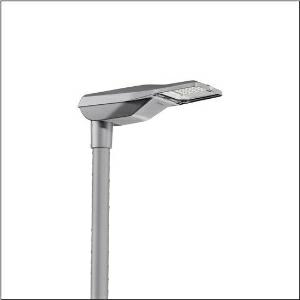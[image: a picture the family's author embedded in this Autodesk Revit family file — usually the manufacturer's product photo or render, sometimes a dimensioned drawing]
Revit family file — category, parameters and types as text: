
# Revit family: streetlight_sl_21_iq_micro___st0_8a_5xe1c31d08db_b6ee
name_source: partatom
category: Lighting Fixtures
units: mm (PartAtom-declared; Revit-internal decimal feet)

## family parameters
Cut with Voids When Loaded = No
Host = Face
Light Source = No
Part Type = Normal
Room Calculation Point = No
Round Connector Dimension = Use Diameter
Shared = No

## types (1)
- --- (1 x LED, 4810 lm, 36.4 W, 3000K)
    Apparent Load = 36 VA
    CIE Flux Codes = 38 75 97 100 100
    Color Rendering = 70
    Color Temperature = 3000K
    Default Elevation = 1800 mm
    Description = Streetlight SL 21 iQ micro, mast luminaire, primary light control with lens, of PMMA, primary optical cover: cover, of toughened safety glass, transparent, light distribution: ST0.8a, light emission: direct distribution, primary light characteristic: asymmetric, installation type: post-top, side-entry, LED, High Power LED, rated luminous flux: 4.810lm, luminous efficacy: 132lm/W, light colour: 730, colour temperature: 3000K, control gear: iQ-Comfort, control: Auto-Match, Temp-Guard, Lumen-Switch, Night-Set, Smart-Wire, Light-Fading, Desk-Remote (wireless, voltage-free reading and setting of iQ features in the workshop via application-optimized NFC function/RFID function), optimised constant luminous flux control (CLO 2.0), pre-setting: linear dimming characteristic, mains connection: 220..240V, AC, 50/60Hz, start of lifetime: 36W, end of service life: 38W, reduction: 16W, luminaire housing, of diecast aluminium, powder-coated, Siteco® metallic grey (DB 702S), corrosivity category C5 mid according to DIN EN ISO 12944, please order mast flange separately, inclination adjustable: 0°, 5°, 10°, 15°, sealing non-destructively replaceable, multi-level sealing system, length: 528mm, width: 235mm, height: 110mm, mast flange for spigot size: 42mm (side-entry): 5XC10008XM4, 60/48mm (side-entry/post-top): 5XC10108XM2, 76/60mm (side-entry/post-top): 5XC10108XM1, protection rating (complete): IP66, insulation class (complete): insulation class II (safety insulation), certification: CE, ENEC, ENEC+, VDE, impact resistance: IK10, permissible operating ambient temperature for outdoor applications: -40..+50°C, standard-compliant lighting for roads and squares, packaging unit: 1 piece

Light Distribution: ST0.8a
    Height = 110 mm
    Lamp = 1 x LED
    Lamp Light Flux = 4810 lm
    Lamp Power = 36.4 W
    Lamp count = 1
    Length = 528 mm
    Luminous efficacy = 132 lm/W
    Manufacturer = Siteco
    ModVariant = No
    Model = 5XE1C31D08DB
    Number of Poles = 1
    OnlyDefault = Yes
    Power Factor = 1
    Product Name = Streetlight SL 21 iQ micro | ST0.8a
    Product group = mast luminaire | pylon top
    ProductGroupID = 6100
    Protection Class = Protection class II
    Protection Degree = IP 66
    RLX_Detail_Level = 1
    RLX_Emergency_Light_Flux = 0 lm
    RLX_Emergency_Type = 0
    RLX_Emergency_Type_DB = No
    RlxData = <blob elided: 98957 chars, md5=221f48d3>
    Socket = socket
    Standby Power = 0 W
    System Light Flux = 4810 lm
    System Power = 36 W
    Type Comments = factory setting: luminous flux: 100 % | dim-lin: 254 | 715 mA
    Type Image = l_1006881.jpg
    URL = http://relux.com
    VarID = @adj_154618
    Voltage = 0 V
    Weight = 0.00 kg
    Width = 235 mm

## geometry (parser evidence)
native form markers: Blend x4, Sweep x10
no freeform markers — native parametric forms only
